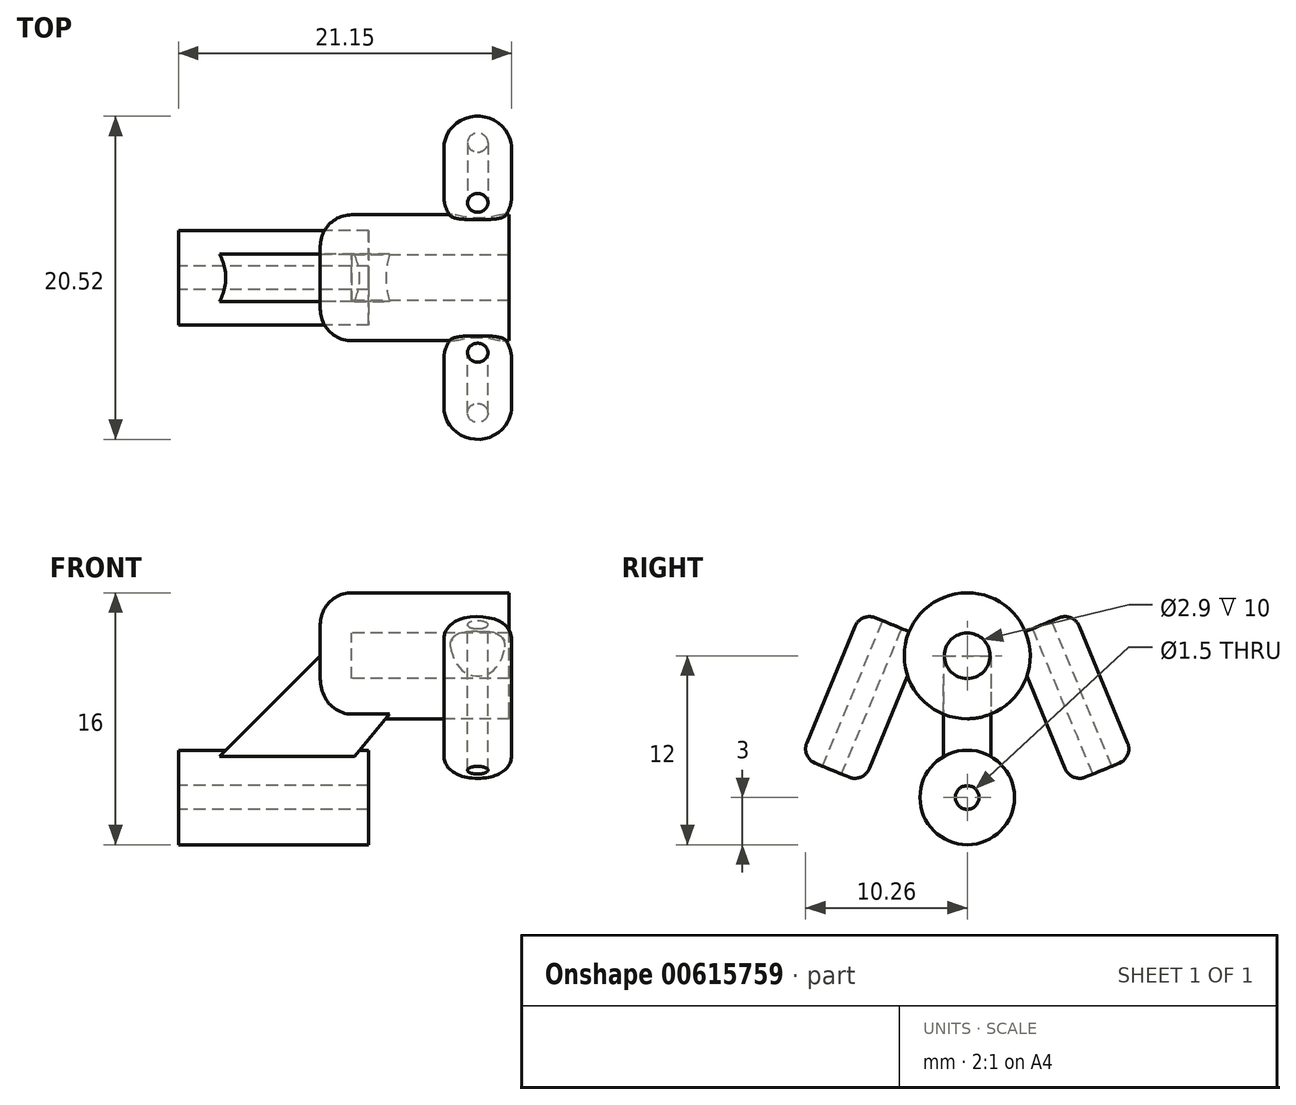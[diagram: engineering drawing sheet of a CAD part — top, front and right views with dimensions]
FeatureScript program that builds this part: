
annotation { "Feature Type Name" : "Feature", "Feature Type Description" : "" }
export const myFeature = defineFeature(function(context is Context, id is Id, definition is map)
    precondition{}
    {
        {
            var Q0;
            Q0=qCreatedBy(makeId("Right.planeOp"),FACE);
            var sketch = newSketch(context, id + "F0", { "sketchPlane" : qUnion([Q0])});
            skCircle(sketch, "E0", {"center": v(0, 0) * mm, "radius": 4 * mm});
            skSolve(sketch);
        }
        {
            var Q0;
            Q0 = qSketchRegion(id + "F0", true);
            extrude(context, id + "F1", {"entities" : qUnion([Q0]), "depth" : 2 * mm, "offsetDistance" : 25 * mm});
        }
        {
            var Q0;
            Q0=makeQuery(id+"F1.opExtrude","CAP_FACE",FACE,{"disambiguationData":[OSD([sQuery(id+"F0.wireOp",EDGE,"E0")])],"isStart":false});
            var sketch = newSketch(context, id + "F2", { "sketchPlane" : qUnion([Q0])});
            skCircle(sketch, "E1", {"center": v(0, 0) * mm, "radius": 1.45 * mm});
            skCircle(sketch, "E2.0", {"center": v(0, 0) * mm, "radius": 4 * mm});
            skSolve(sketch);
        }
        {
            var Q0;
            Q0 = qSketchRegion(id + "F2", true);
            extrude(context, id + "F3", {"entities" : qUnion([Q0]), "operationType" : NewBodyOperationType.ADD, "depth" : 10 * mm, "offsetDistance" : 25 * mm});
        }
        {
            var Q0;
            Q0=qCreatedBy(makeId("Front.planeOp"),FACE);
            var sketch = newSketch(context, id + "F4", { "sketchPlane" : qUnion([Q0])});
            skLineSegment(sketch, "E3", {"start": v(0, 0) * mm, "end": v(-9, -9) * mm});
            skLineSegment(sketch, "E4", {"start": v(-9, -9) * mm, "end": v(0, -9) * mm});
            skLineSegment(sketch, "E5", {"start": v(0, -9) * mm, "end": v(5, -3) * mm});
            skLineSegment(sketch, "E6", {"start": v(0, 0) * mm, "end": v(0, -3) * mm});
            skLineSegment(sketch, "E7", {"start": v(0, -3) * mm, "end": v(5, -3) * mm});
            skSolve(sketch);
        }
        {
            var Q0;
            Q0 = qSketchRegion(id + "F4", true);
            extrude(context, id + "F5", {"entities" : qUnion([Q0]), "operationType" : NewBodyOperationType.ADD, "endBound" : BoundingType.SYMMETRIC, "depth" : 3 * mm, "offsetDistance" : 25 * mm});
        }
        {
            var Q0;
            Q0=makeQuery(id+"F5.opExtrude","SWEPT_EDGE",EDGE,{"disambiguationData":[OSD([sQuery(id+"F4.wireOp",EDGE,"E3"),sQuery(id+"F4.wireOp",EDGE,"E4")])]});
            cPoint(context, id + "F6", {"entities" : qUnion([Q0]), "parameter" : 0.5});
        }
        {
            var Q0;
            Q0 = qCreatedBy(id + "F6" ,VERTEX);
            var Q1;
            Q1=qCreatedBy(makeId("Right.planeOp"),FACE);
            cPlane(context, id + "F7", {"entities" : qUnion([Q0, Q1]), "cplaneType" : CPlaneType.PLANE_POINT, "offset" : 25 * mm, "width" : 150 * mm, "height" : 150 * mm});
        }
        {
            var Q0;
            Q0=qCreatedBy(id+"F7.planeOp",FACE);
            var sketch = newSketch(context, id + "F8", { "sketchPlane" : qUnion([Q0])});
            skPoint(sketch, "E8.0", {"position": v(0, -9) * mm});
            skCircle(sketch, "E9", {"center": v(0, -9) * mm, "radius": 0.65 * mm, "construction": true});
            skCircle(sketch, "E10", {"center": v(0, -9) * mm, "radius": 3 * mm});
            skSolve(sketch);
        }
        {
            var Q0;
            Q0 = qSketchRegion(id + "F8", true);
            extrude(context, id + "F9", {"entities" : qUnion([Q0]), "operationType" : NewBodyOperationType.ADD, "depth" : 12.07 * mm, "offsetDistance" : 25 * mm});
        }
        {
            var Q0;
            Q0=makeQuery(id+"F9.opExtrude","CAP_FACE",FACE,{"disambiguationData":[OSD([sQuery(id+"F8.wireOp",EDGE,"E10")])],"isStart":true});
            var sketch = newSketch(context, id + "F10", { "sketchPlane" : qUnion([Q0])});
            skCircle(sketch, "E11", {"center": v(0, -9) * mm, "radius": 0.75 * mm});
            skSolve(sketch);
        }
        {
            var Q0;
            Q0 = qSketchRegion(id + "F10", true);
            extrude(context, id + "F11", {"entities" : qUnion([Q0]), "operationType" : NewBodyOperationType.REMOVE, "oppositeDirection" : true, "depth" : 25 * mm, "offsetDistance" : 25 * mm});
        }
        {
            var Q0;
            Q0=qCreatedBy(makeId("Top.planeOp"),FACE);
            var Q1;
            Q1=makeQuery(id+"F1.opExtrude","CAP_EDGE",EDGE,{"disambiguationData":[OSD([sQuery(id+"F0.wireOp",EDGE,"E0")])],"isStart":true});
            cPlane(context, id + "F12", {"entities" : qUnion([Q0, Q1]), "cplaneType" : CPlaneType.LINE_ANGLE, "offset" : 25 * mm, "angle" : 22.5 * degree, "oppositeDirection" : true, "width" : 150 * mm, "height" : 150 * mm});
        }
        {
            var Q0;
            Q0=makeQuery(id+"F1.opExtrude","CAP_EDGE",EDGE,{"disambiguationData":[OSD([sQuery(id+"F0.wireOp",EDGE,"E0")])],"isStart":true});
            fillet(context, id + "F13", {"entities" : qUnion([Q0]), "radius" : 2 * mm, "tangentPropagation" : true, "allowEdgeOverflow" : false});
        }
        {
            var Q0;
            Q0=qCreatedBy(id+"F12.planeOp",FACE);
            var sketch = newSketch(context, id + "F14", { "sketchPlane" : qUnion([Q0])});
            skCircle(sketch, "E12", {"center": v(10, 5.15) * mm, "radius": 0.65 * mm});
            skCircle(sketch, "E13", {"center": v(10, 5.15) * mm, "radius": 2.15 * mm});
            skLineSegment(sketch, "E14", {"start": v(7.98, 3) * mm, "end": v(10, 3) * mm, "construction": true});
            skSolve(sketch);
        }
        {
            var Q0;
            Q0 = qSketchRegion(id + "F14", true);
            extrude(context, id + "F15", {"entities" : qUnion([Q0]), "depth" : 10 * mm, "offsetDistance" : 25 * mm});
        }
        {
            var Q0;
            Q0=makeQuery(id+"F15.opExtrude","CAP_EDGE",EDGE,{"disambiguationData":[OSD([sQuery(id+"F14.wireOp",EDGE,"E13")])],"isStart":false});
            var Q1;
            Q1=makeQuery(id+"F15.opExtrude","CAP_EDGE",EDGE,{"disambiguationData":[OSD([sQuery(id+"F14.wireOp",EDGE,"E13")])],"isStart":true});
            fillet(context, id + "F16", {"entities" : qUnion([Q0, Q1]), "radius" : 1 * mm, "tangentPropagation" : true, "allowEdgeOverflow" : false});
        }
        {
            var Q0;
            Q0=makeQuery(id+"F15.opExtrude","SWEPT_BODY",BODY,{"disambiguationData":[OSD([sQuery(id+"F14.wireOp",EDGE,"E12"),sQuery(id+"F14.wireOp",EDGE,"E13")])]});
            var Q1;
            Q1=qCreatedBy(makeId("Front.planeOp"),FACE);
            mirror(context, id + "F17", {"operationType" : NewBodyOperationType.ADD, "entities" : qUnion([Q0]), "mirrorPlane" : qUnion([Q1])});
        }
    });
